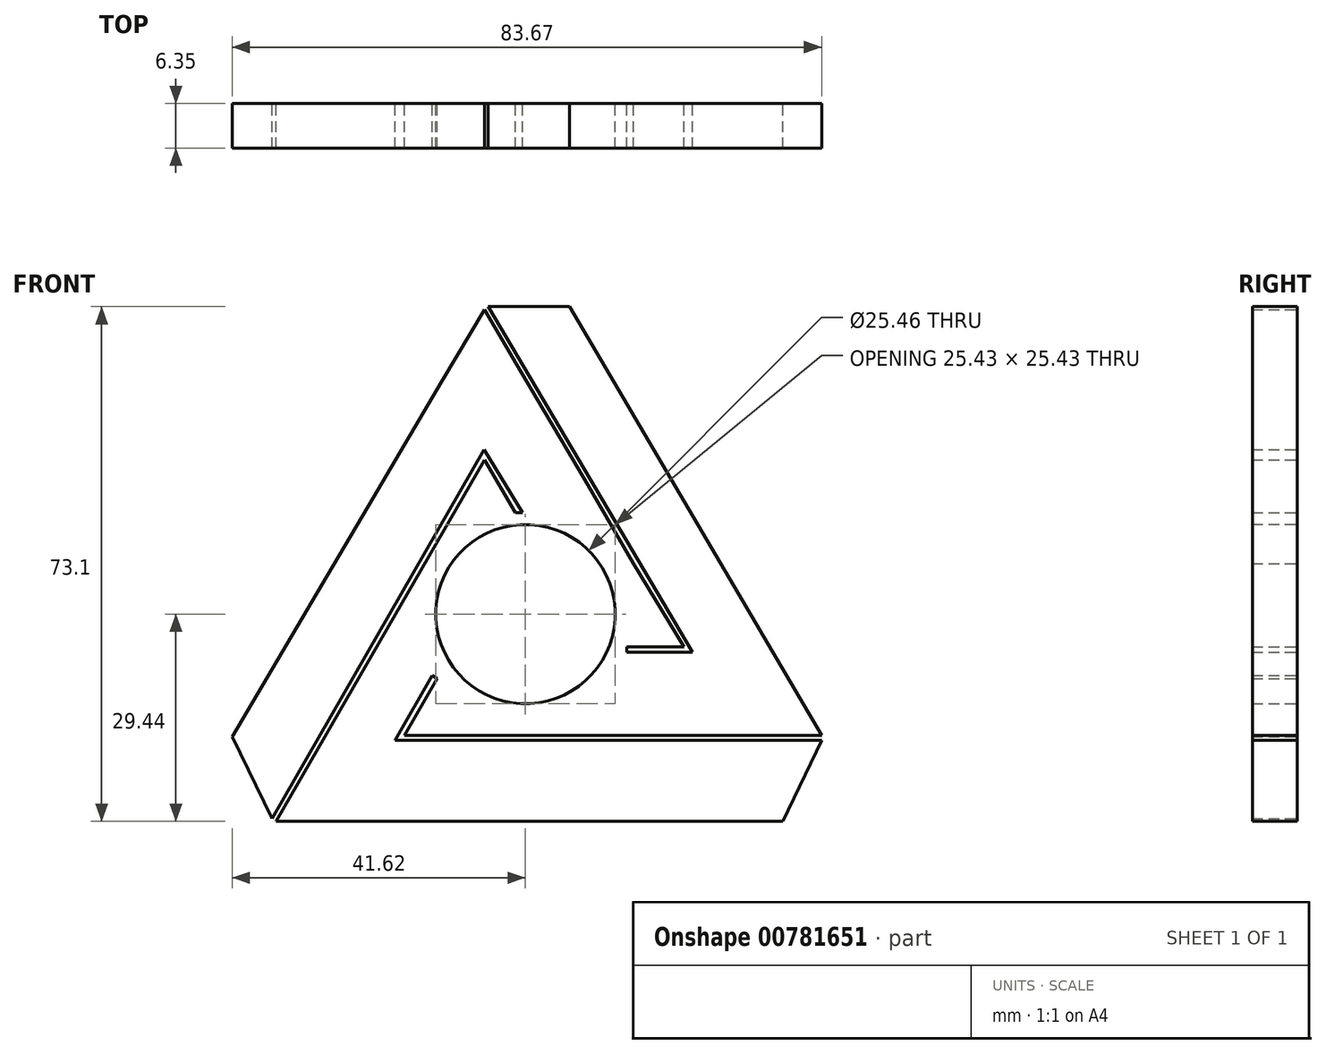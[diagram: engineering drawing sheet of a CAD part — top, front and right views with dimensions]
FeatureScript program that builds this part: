
annotation { "Feature Type Name" : "Feature", "Feature Type Description" : "" }
export const myFeature = defineFeature(function(context is Context, id is Id, definition is map)
    precondition{}
    {
        {
            var Q0;
            Q0=qCreatedBy(makeId("Front.planeOp"),FACE);
            var sketch = newSketch(context, id + "F0", { "sketchPlane" : qUnion([Q0])});
            skCircle(sketch, "E0", {"center": v(0, 0) * mm, "radius": 12.7 * mm});
            skLineSegment(sketch, "E1", {"start": v(11.81, -4.67) * mm, "end": v(22.5, -4.67) * mm});
            skLineSegment(sketch, "E2", {"start": v(22.5, -4.67) * mm, "end": v(15.33, 7.17) * mm});
            skLineSegment(sketch, "E3", {"start": v(15.33, 7.17) * mm, "end": v(8.83, 18.3) * mm});
            skLineSegment(sketch, "E4", {"start": v(8.83, 18.3) * mm, "end": v(5.1, 24.7) * mm});
            skLineSegment(sketch, "E5", {"start": v(5.1, 24.7) * mm, "end": v(2.52, 29.07) * mm});
            skLineSegment(sketch, "E6", {"start": v(2.52, 29.07) * mm, "end": v(-1.21, 35.4) * mm});
            skLineSegment(sketch, "E7", {"start": v(-1.21, 35.4) * mm, "end": v(-5.78, 43.25) * mm});
            skLineSegment(sketch, "E8", {"start": v(-5.78, 43.25) * mm, "end": v(-11.87, 33.03) * mm});
            skLineSegment(sketch, "E9", {"start": v(-11.87, 33.03) * mm, "end": v(-21.64, 16.47) * mm});
            skLineSegment(sketch, "E10", {"start": v(-21.64, 16.47) * mm, "end": v(-28.84, 4.26) * mm});
            skLineSegment(sketch, "E11", {"start": v(-28.84, 4.26) * mm, "end": v(-37.36, -10.18) * mm});
            skLineSegment(sketch, "E12", {"start": v(-37.36, -10.18) * mm, "end": v(-41.62, -17.4) * mm});
            skLineSegment(sketch, "E13", {"start": v(-41.62, -17.4) * mm, "end": v(-36, -29.02) * mm});
            skLineSegment(sketch, "E14", {"start": v(-36, -29.02) * mm, "end": v(-5.87, 23.38) * mm});
            skLineSegment(sketch, "E15", {"start": v(-5.87, 23.38) * mm, "end": v(0.66, 12.68) * mm});
            skLineSegment(sketch, "E16", {"start": v(-11.43, -5.53) * mm, "end": v(-18.52, -17.93) * mm});
            skLineSegment(sketch, "E17", {"start": v(-18.52, -17.93) * mm, "end": v(42.05, -17.93) * mm});
            skLineSegment(sketch, "E18", {"start": v(42.05, -17.93) * mm, "end": v(36.53, -29.44) * mm});
            skLineSegment(sketch, "E19", {"start": v(36.53, -29.44) * mm, "end": v(-35.37, -29.44) * mm});
            skLineSegment(sketch, "E20", {"start": v(-35.37, -29.44) * mm, "end": v(-5.82, 21.92) * mm});
            skLineSegment(sketch, "E21", {"start": v(-5.82, 21.92) * mm, "end": v(-0.44, 12.7) * mm});
            skLineSegment(sketch, "E22", {"start": v(42.05, -17.25) * mm, "end": v(-17.19, -17.25) * mm});
            skLineSegment(sketch, "E23", {"start": v(-17.19, -17.25) * mm, "end": v(-10.98, -6.38) * mm});
            skLineSegment(sketch, "E24", {"start": v(42.05, -17.25) * mm, "end": v(6.27, 43.66) * mm});
            skLineSegment(sketch, "E25", {"start": v(6.27, 43.66) * mm, "end": v(-5.33, 43.66) * mm});
            skLineSegment(sketch, "E26", {"start": v(-5.33, 43.66) * mm, "end": v(23.71, -5.42) * mm});
            skLineSegment(sketch, "E27", {"start": v(23.71, -5.42) * mm, "end": v(11.48, -5.42) * mm});
            skCircle(sketch, "E28", {"center": v(0, 0) * mm, "radius": 12.73 * mm});
            skLineSegment(sketch, "E29", {"start": v(-10.98, -6.38) * mm, "end": v(-12.56, -9.14) * mm});
            skLineSegment(sketch, "E30", {"start": v(-12.56, -9.14) * mm, "end": v(-13.26, -8.73) * mm});
            skLineSegment(sketch, "E31", {"start": v(-13.26, -8.73) * mm, "end": v(-11.43, -5.53) * mm});
            skLineSegment(sketch, "E32", {"start": v(-13.26, -8.73) * mm, "end": v(-12.56, -9.14) * mm});
            skLineSegment(sketch, "E33", {"start": v(11.81, -4.67) * mm, "end": v(14.4, -4.67) * mm});
            skLineSegment(sketch, "E34", {"start": v(14.4, -5.42) * mm, "end": v(11.48, -5.42) * mm});
            skLineSegment(sketch, "E35", {"start": v(14.4, -5.42) * mm, "end": v(14.4, -4.67) * mm});
            skLineSegment(sketch, "E36", {"start": v(-0.44, 12.7) * mm, "end": v(-1.45, 14.43) * mm});
            skLineSegment(sketch, "E37", {"start": v(0.64, 12.71) * mm, "end": v(0.66, 12.68) * mm});
            skPoint(sketch, "E38.end.orphan", {"position": v(-0.44, 14.43) * mm});
            skLineSegment(sketch, "E39", {"start": v(-1.45, 14.43) * mm, "end": v(-0.4, 14.43) * mm});
            skLineSegment(sketch, "E40", {"start": v(-0.4, 14.43) * mm, "end": v(0.64, 12.71) * mm});
            skSolve(sketch);
        }
        {
            var Q0;
            Q0 = qSketchRegion(id + "F0", true);
            extrude(context, id + "F1", {"entities" : qUnion([Q0]), "depth" : 6.35 * mm, "offsetDistance" : 25.4 * mm});
        }
    });
